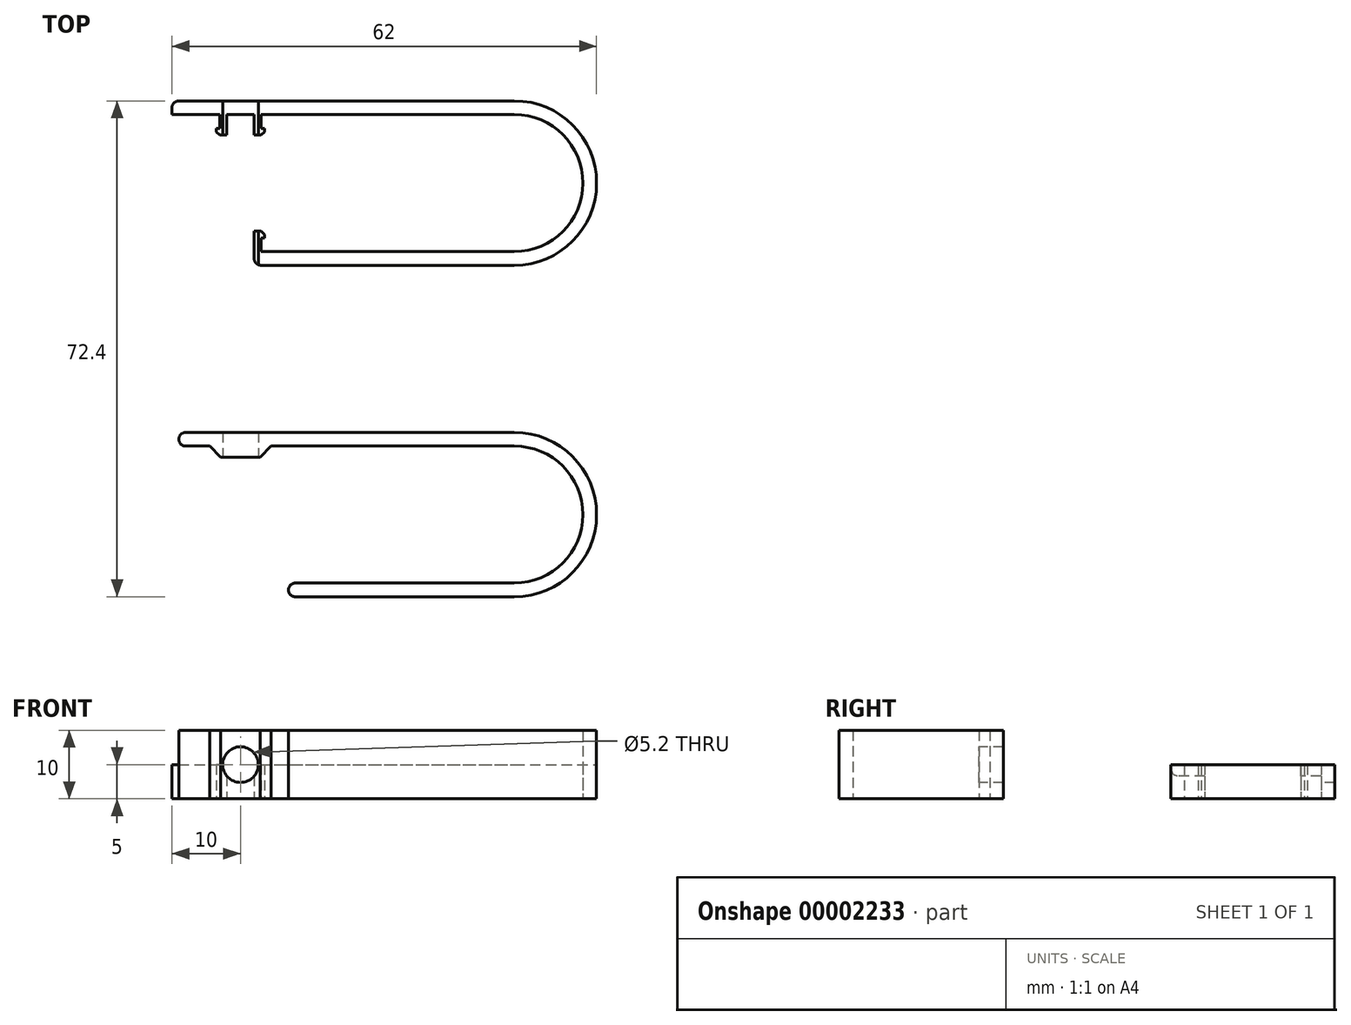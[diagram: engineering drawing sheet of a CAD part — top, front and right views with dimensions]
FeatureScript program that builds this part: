
annotation { "Feature Type Name" : "Feature", "Feature Type Description" : "" }
export const myFeature = defineFeature(function(context is Context, id is Id, definition is map)
    precondition{}
    {
        {
            var Q0;
            Q0=qCreatedBy(makeId("Top.planeOp"),FACE);
            var sketch = newSketch(context, id + "F0", { "sketchPlane" : qUnion([Q0])});
            skLineSegment(sketch, "E0", {"start": v(-10, 0) * mm, "end": v(-10, 2) * mm});
            skLineSegment(sketch, "E1", {"start": v(-10, 2) * mm, "end": v(40, 2) * mm});
            skArc(sketch, "E2", {"start": v(40, -22) * mm, "mid": v(52, -10) * mm, "end": v(40, 2) * mm});
            skLineSegment(sketch, "E3", {"start": v(-10, 0) * mm, "end": v(-3, 0) * mm});
            skLineSegment(sketch, "E4", {"start": v(-3, 0) * mm, "end": v(-3, -2) * mm});
            skLineSegment(sketch, "E5", {"start": v(-3, -2) * mm, "end": v(-3.5, -2) * mm});
            skLineSegment(sketch, "E6", {"start": v(-3.5, -2) * mm, "end": v(-3.5, -2.5) * mm});
            skLineSegment(sketch, "E7", {"start": v(-3.5, -2.5) * mm, "end": v(-3, -3) * mm});
            skLineSegment(sketch, "E8", {"start": v(-3, -3) * mm, "end": v(-2, -3) * mm});
            skLineSegment(sketch, "E9", {"start": v(-2, -3) * mm, "end": v(-2, 0) * mm});
            skLineSegment(sketch, "E10", {"start": v(-2, 0) * mm, "end": v(2, 0) * mm});
            skLineSegment(sketch, "E11", {"start": v(2, 0) * mm, "end": v(2, -3) * mm});
            skLineSegment(sketch, "E12", {"start": v(2, -3) * mm, "end": v(3, -3) * mm});
            skLineSegment(sketch, "E13", {"start": v(3, -3) * mm, "end": v(3.5, -2.5) * mm});
            skLineSegment(sketch, "E14", {"start": v(3.5, -2.5) * mm, "end": v(3.5, -2) * mm});
            skLineSegment(sketch, "E15", {"start": v(3.5, -2) * mm, "end": v(3, -2) * mm});
            skLineSegment(sketch, "E16", {"start": v(3, -2) * mm, "end": v(3, 0) * mm});
            skLineSegment(sketch, "E17", {"start": v(3, 0) * mm, "end": v(40, 0) * mm});
            skLineSegment(sketch, "E18", {"start": v(40, -22) * mm, "end": v(2, -22) * mm});
            skLineSegment(sketch, "E19", {"start": v(2, -22) * mm, "end": v(2, -17) * mm});
            skLineSegment(sketch, "E20", {"start": v(2, -17) * mm, "end": v(3, -17) * mm});
            skLineSegment(sketch, "E21", {"start": v(3, -17) * mm, "end": v(3.5, -17.5) * mm});
            skLineSegment(sketch, "E22", {"start": v(3.5, -17.5) * mm, "end": v(3.5, -18) * mm});
            skLineSegment(sketch, "E23", {"start": v(3.5, -18) * mm, "end": v(3, -18) * mm});
            skLineSegment(sketch, "E24", {"start": v(3, -18) * mm, "end": v(3, -20) * mm});
            skLineSegment(sketch, "E25", {"start": v(3, -20) * mm, "end": v(40, -20) * mm});
            skArc(sketch, "E26", {"start": v(40, -20) * mm, "mid": v(50, -10) * mm, "end": v(40, 0) * mm});
            skPoint(sketch, "E27", {"position": v(0, 0) * mm});
            skSolve(sketch);
        }
        {
            var Q0;
            Q0 = qSketchRegion(id + "F0", true);
            extrude(context, id + "F1", {"entities" : qUnion([Q0]), "depth" : 5 * mm});
        }
        {
            var Q0;
            Q0=makeQuery(id+"F1.opExtrude","SWEPT_EDGE",EDGE,{"disambiguationData":[OSD([sQuery(id+"F0.wireOp",EDGE,"E0"),sQuery(id+"F0.wireOp",EDGE,"E1")])]});
            var Q1;
            Q1=makeQuery(id+"F1.opExtrude","SWEPT_EDGE",EDGE,{"disambiguationData":[OSD([sQuery(id+"F0.wireOp",EDGE,"E18"),sQuery(id+"F0.wireOp",EDGE,"E19")])]});
            fillet(context, id + "F2", {"entities" : qUnion([Q0, Q1]), "radius" : 1 * mm, "tangentPropagation" : true, "allowEdgeOverflow" : false});
        }
        {
            var Q0;
            Q0=qCreatedBy(makeId("Top.planeOp"),FACE);
            var sketch = newSketch(context, id + "F3", { "sketchPlane" : qUnion([Q0])});
            skLineSegment(sketch, "E28", {"start": v(40, -46.4) * mm, "end": v(-8, -46.4) * mm});
            skLineSegment(sketch, "E29", {"start": v(-8, -48.4) * mm, "end": v(-4.5, -48.4) * mm});
            skLineSegment(sketch, "E30", {"start": v(-4.5, -48.4) * mm, "end": v(-2.9, -50) * mm});
            skLineSegment(sketch, "E31", {"start": v(-2.9, -50) * mm, "end": v(2.9, -50) * mm});
            skLineSegment(sketch, "E32", {"start": v(2.9, -50) * mm, "end": v(4.5, -48.4) * mm});
            skLineSegment(sketch, "E33", {"start": v(4.5, -48.4) * mm, "end": v(40, -48.4) * mm});
            skLineSegment(sketch, "E34", {"start": v(40, -68.4) * mm, "end": v(8, -68.4) * mm});
            skLineSegment(sketch, "E35", {"start": v(8, -70.4) * mm, "end": v(40, -70.4) * mm});
            skArc(sketch, "E36", {"start": v(40, -68.4) * mm, "mid": v(50, -58.4) * mm, "end": v(40, -48.4) * mm});
            skArc(sketch, "E37", {"start": v(40, -70.4) * mm, "mid": v(52, -58.4) * mm, "end": v(40, -46.4) * mm});
            skArc(sketch, "E38", {"start": v(8, -68.4) * mm, "mid": v(7, -69.4) * mm, "end": v(8, -70.4) * mm});
            skPoint(sketch, "E39", {"position": v(0, -50) * mm});
            skArc(sketch, "E40", {"start": v(-8, -46.4) * mm, "mid": v(-9, -47.4) * mm, "end": v(-8, -48.4) * mm});
            skSolve(sketch);
        }
        {
            var Q0;
            Q0 = qSketchRegion(id + "F3", true);
            extrude(context, id + "F4", {"entities" : qUnion([Q0]), "depth" : 10 * mm});
        }
        {
            var Q0;
            Q0=makeQuery(id+"F4.opExtrude","SWEPT_FACE",FACE,{"disambiguationData":[OSD([sQuery(id+"F3.wireOp",EDGE,"E31")])]});
            var sketch = newSketch(context, id + "F5", { "sketchPlane" : qUnion([Q0])});
            skCircle(sketch, "E41", {"center": v(0, 5) * mm, "radius": 2.6 * mm});
            skPoint(sketch, "E42", {"position": v(2.9, 5) * mm});
            skSolve(sketch);
        }
        {
            var Q0;
            Q0 = qSketchRegion(id + "F5", true);
            extrude(context, id + "F6", {"entities" : qUnion([Q0]), "operationType" : NewBodyOperationType.REMOVE, "endBound" : BoundingType.THROUGH_ALL, "oppositeDirection" : true, "depth" : 25 * mm});
        }
    });
